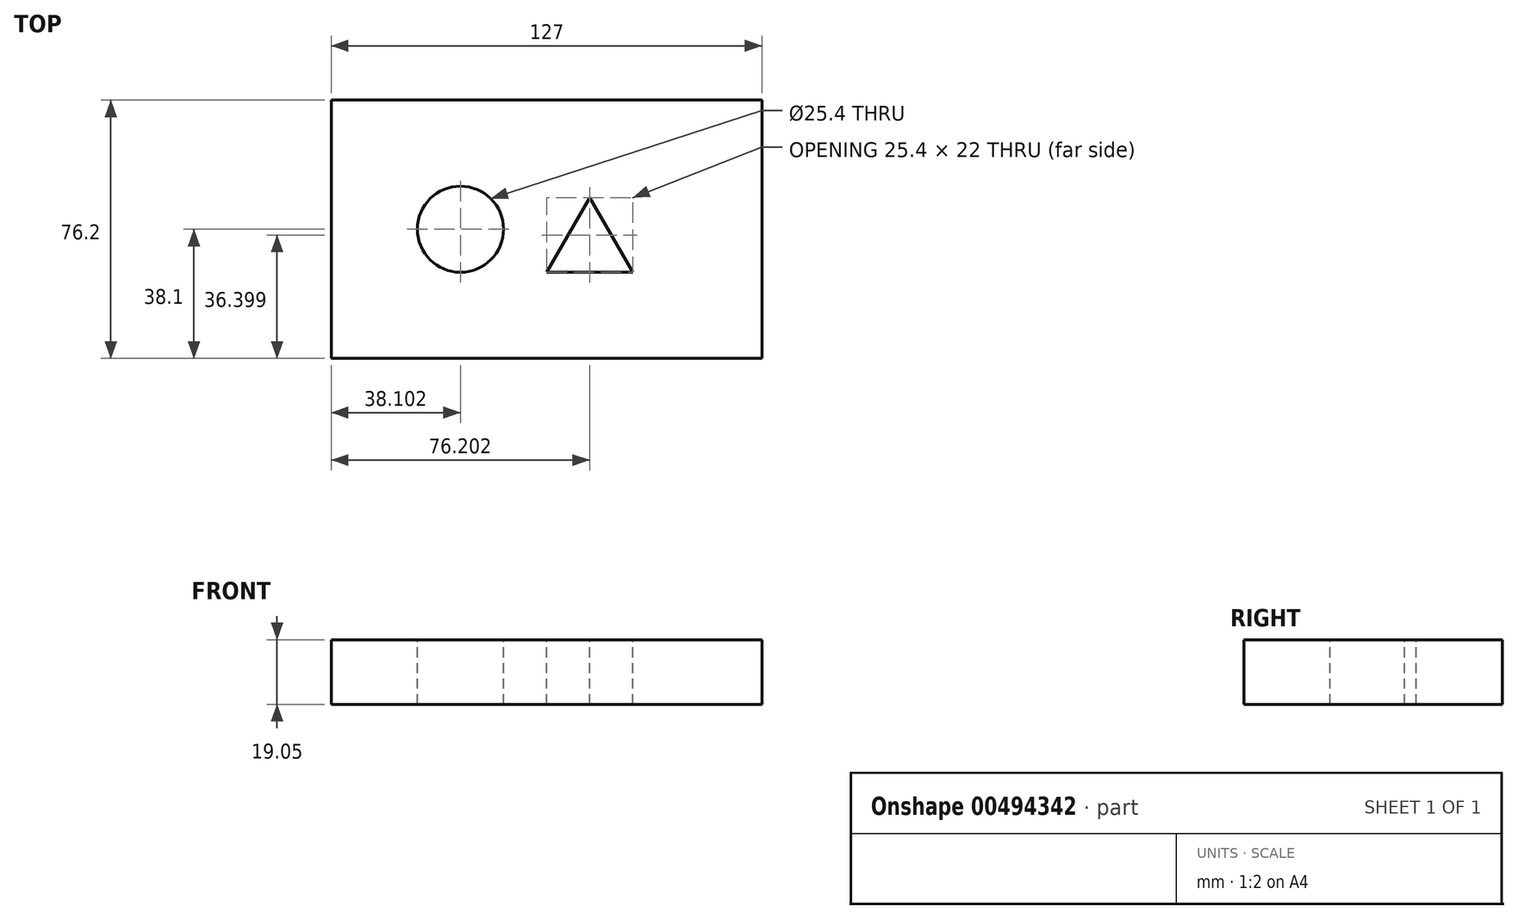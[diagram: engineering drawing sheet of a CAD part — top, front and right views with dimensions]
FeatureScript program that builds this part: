
annotation { "Feature Type Name" : "Feature", "Feature Type Description" : "" }
export const myFeature = defineFeature(function(context is Context, id is Id, definition is map)
    precondition{}
    {
        {
            var Q0;
            Q0=qCreatedBy(makeId("Front.planeOp"),FACE);
            var sketch = newSketch(context, id + "F0", { "sketchPlane" : qUnion([Q0])});
            skLineSegment(sketch, "E0.bottom", {"start": v(-60.38, 33.19) * mm, "end": v(66.62, 33.19) * mm});
            skLineSegment(sketch, "E0.top", {"start": v(-60.38, 14.14) * mm, "end": v(66.62, 14.14) * mm});
            skLineSegment(sketch, "E0.left", {"start": v(-60.38, 33.19) * mm, "end": v(-60.38, 14.14) * mm});
            skLineSegment(sketch, "E0.right", {"start": v(66.62, 33.19) * mm, "end": v(66.62, 14.14) * mm});
            skSolve(sketch);
        }
        {
            var Q0;
            Q0 = qSketchRegion(id + "F0", true);
            extrude(context, id + "F1", {"entities" : qUnion([Q0]), "depth" : 76.2 * mm});
        }
        {
            var Q0;
            Q0=makeQuery(id+"F1.opExtrude","SWEPT_FACE",FACE,{"disambiguationData":[OSD([sQuery(id+"F0.wireOp",EDGE,"E0.bottom")])]});
            var sketch = newSketch(context, id + "F2", { "sketchPlane" : qUnion([Q0])});
            skCircle(sketch, "E1", {"center": v(-22.28, -38.1) * mm, "radius": 12.7 * mm});
            skSolve(sketch);
        }
        {
            var Q0;
            Q0=makeQuery(id+"F2.imprint","IMPRINT",FACE,{"disambiguationData":[TD([[makeQuery(id+"F2.imprint","IMPRINT",EDGE,{"derivedFrom":sQuery(id+"F2.wireOp",EDGE,"E1")}),1.0]])]});
            extrude(context, id + "F3", {"entities" : qUnion([Q0]), "operationType" : NewBodyOperationType.REMOVE, "oppositeDirection" : true, "depth" : 25.4 * mm});
        }
        {
            var Q0;
            Q0=makeQuery(id+"F1.opExtrude","SWEPT_FACE",FACE,{"disambiguationData":[OSD([sQuery(id+"F0.wireOp",EDGE,"E0.bottom")])]});
            var sketch = newSketch(context, id + "F4", { "sketchPlane" : qUnion([Q0])});
            skCircle(sketch, "E2.cCircle", {"center": v(15.82, -43.47) * mm, "radius": 7.33 * mm, "construction": true});
            skLineSegment(sketch, "E2.0", {"start": v(15.82, -28.8) * mm, "end": v(28.52, -50.8) * mm});
            skLineSegment(sketch, "E2.1", {"start": v(28.52, -50.8) * mm, "end": v(3.12, -50.8) * mm});
            skLineSegment(sketch, "E2.2", {"start": v(3.12, -50.8) * mm, "end": v(15.82, -28.8) * mm});
            skPoint(sketch, "E2.0.midPoint", {"position": v(22.17, -39.8) * mm});
            skSolve(sketch);
        }
        {
            var Q0;
            Q0=makeQuery(id+"F4.imprint","IMPRINT",FACE,{"disambiguationData":[TD([[makeQuery(id+"F4.imprint","IMPRINT",EDGE,{"derivedFrom":sQuery(id+"F4.wireOp",EDGE,"E2.0")}),-1.0]])]});
            extrude(context, id + "F5", {"entities" : qUnion([Q0]), "operationType" : NewBodyOperationType.REMOVE, "oppositeDirection" : true, "depth" : 25.4 * mm});
        }
    });
